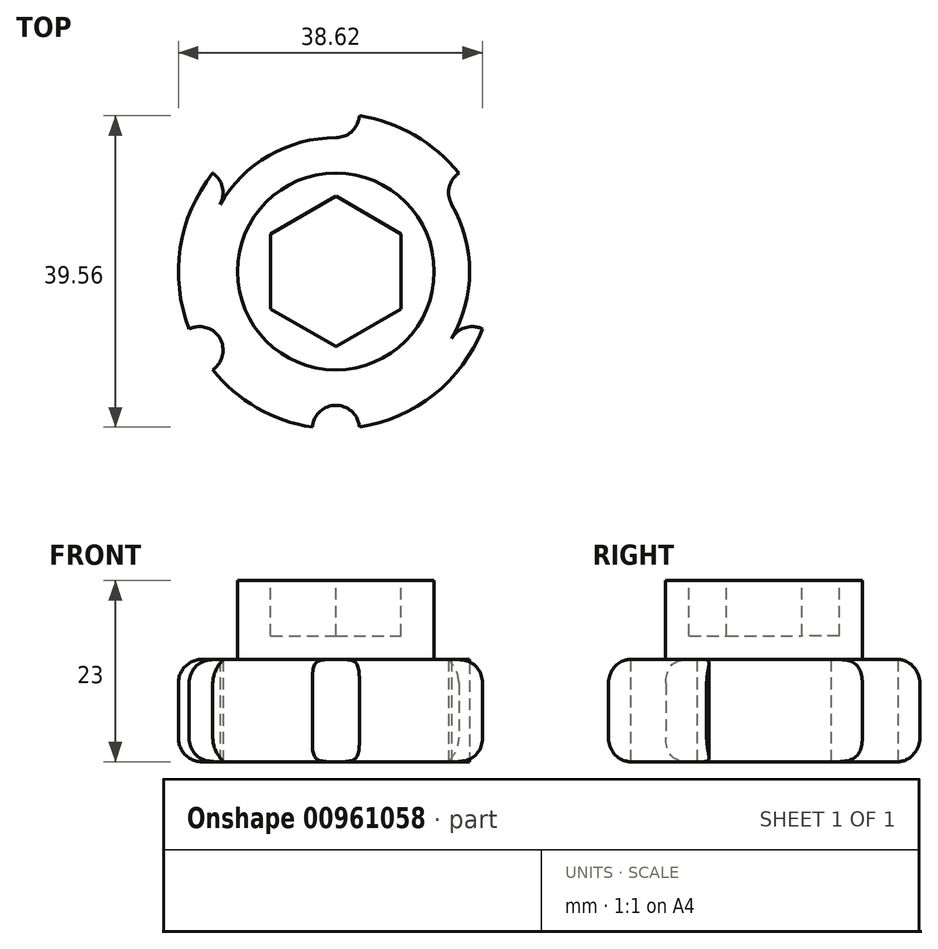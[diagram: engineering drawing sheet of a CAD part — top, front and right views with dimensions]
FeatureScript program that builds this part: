
annotation { "Feature Type Name" : "Feature", "Feature Type Description" : "" }
export const myFeature = defineFeature(function(context is Context, id is Id, definition is map)
    precondition{}
    {
        {
            var Q0;
            Q0=qCreatedBy(makeId("Top.planeOp"),FACE);
            var sketch = newSketch(context, id + "F0", { "sketchPlane" : qUnion([Q0])});
            skCircle(sketch, "E0", {"center": v(0, 0) * mm, "radius": 20 * mm});
            skSolve(sketch);
        }
        {
            var Q0;
            Q0 = qSketchRegion(id + "F0", true);
            extrude(context, id + "F1", {"entities" : qUnion([Q0]), "depth" : 13 * mm, "offsetDistance" : 25 * mm});
        }
        {
            var Q0;
            Q0=makeQuery(id+"F1.opExtrude","CAP_FACE",FACE,{"disambiguationData":[OSD([sQuery(id+"F0.wireOp",EDGE,"E0")])],"isStart":false});
            var sketch = newSketch(context, id + "F2", { "sketchPlane" : qUnion([Q0])});
            skCircle(sketch, "E1", {"center": v(0, 0) * mm, "radius": 12.5 * mm});
            skSolve(sketch);
        }
        {
            var Q0;
            Q0 = qSketchRegion(id + "F2", true);
            extrude(context, id + "F3", {"entities" : qUnion([Q0]), "operationType" : NewBodyOperationType.ADD, "depth" : 10 * mm, "offsetDistance" : 25 * mm});
        }
        {
            var Q0;
            Q0=makeQuery(id+"F1.opExtrude","CAP_EDGE",EDGE,{"disambiguationData":[OSD([sQuery(id+"F0.wireOp",EDGE,"E0")])],"isStart":false});
            var Q1;
            Q1=makeQuery(id+"F1.opExtrude","CAP_EDGE",EDGE,{"disambiguationData":[OSD([sQuery(id+"F0.wireOp",EDGE,"E0")])],"isStart":true});
            fillet(context, id + "F4", {"entities" : qUnion([Q0, Q1]), "radius" : 3 * mm, "tangentPropagation" : true, "allowEdgeOverflow" : false});
        }
        {
            var Q0;
            Q0=makeQuery(id+"F3.opExtrude","CAP_FACE",FACE,{"disambiguationData":[OSD([sQuery(id+"F2.wireOp",EDGE,"E1")])],"isStart":false});
            var sketch = newSketch(context, id + "F5", { "sketchPlane" : qUnion([Q0])});
            skCircle(sketch, "E2.cCircle", {"center": v(0, 0) * mm, "radius": 9.55 * mm, "construction": true});
            skLineSegment(sketch, "E2.0", {"start": v(0, 9.55) * mm, "end": v(8.27, 4.78) * mm});
            skLineSegment(sketch, "E2.1", {"start": v(8.27, 4.78) * mm, "end": v(8.27, -4.77) * mm});
            skLineSegment(sketch, "E2.2", {"start": v(8.27, -4.77) * mm, "end": v(0, -9.55) * mm});
            skLineSegment(sketch, "E2.3", {"start": v(0, -9.55) * mm, "end": v(-8.27, -4.78) * mm});
            skLineSegment(sketch, "E2.4", {"start": v(-8.27, -4.78) * mm, "end": v(-8.27, 4.77) * mm});
            skLineSegment(sketch, "E2.5", {"start": v(-8.27, 4.77) * mm, "end": v(0, 9.55) * mm});
            skSolve(sketch);
        }
        {
            var Q0;
            Q0=makeQuery(id+"F5.imprint","IMPRINT",FACE,{"disambiguationData":[TD([[makeQuery(id+"F5.imprint","IMPRINT",EDGE,{"derivedFrom":sQuery(id+"F5.wireOp",EDGE,"E2.0")}),-1.0]])]});
            extrude(context, id + "F6", {"entities" : qUnion([Q0]), "operationType" : NewBodyOperationType.REMOVE, "oppositeDirection" : true, "depth" : 7 * mm, "offsetDistance" : 25 * mm});
        }
        {
            var Q0;
            Q0=makeQuery(id+"F1.opExtrude","CAP_FACE",FACE,{"disambiguationData":[OSD([sQuery(id+"F0.wireOp",EDGE,"E0")])],"isStart":true});
            var sketch = newSketch(context, id + "F7", { "sketchPlane" : qUnion([Q0])});
            skCircle(sketch, "E3.0", {"center": v(0, 0) * mm, "radius": 20 * mm});
            skCircle(sketch, "E4", {"center": v(0, 20) * mm, "radius": 3 * mm});
            skCircle(sketch, "E5.1.0", {"center": v(-17.32, 10) * mm, "radius": 3 * mm});
            skCircle(sketch, "E5.2.0", {"center": v(-17.32, -10) * mm, "radius": 3 * mm});
            skCircle(sketch, "E5.3.0", {"center": v(0, -20) * mm, "radius": 3 * mm});
            skCircle(sketch, "E5.4.0", {"center": v(17.32, -10) * mm, "radius": 3 * mm});
            skCircle(sketch, "E5.5.0", {"center": v(17.32, 10) * mm, "radius": 3 * mm});
            skSolve(sketch);
        }
        {
            var Q0;
            {var subQ0=sQuery(id+"F7.wireOp",EDGE,"E5.1.0");var subQ1=sQuery(id+"F7.wireOp",EDGE,"E3.0");var subQ2=makeQuery(id+"F7.imprint","INTERSECT",VERTEX,{"disambiguationData":[OD(0.0)],"derivedFrom":[subQ1,subQ0]});Q0=makeQuery(id+"F7.imprint","IMPRINT",FACE,{"disambiguationData":[TD([[makeQuery(id+"F7.imprint","IMPRINT",EDGE,{"disambiguationData":[TD([[subQ2,-1.0]])],"derivedFrom":subQ1}),1.0]])]});}
            var Q1;
            {var subQ0=sQuery(id+"F7.wireOp",EDGE,"E4");var subQ1=sQuery(id+"F7.wireOp",EDGE,"E3.0");var subQ2=makeQuery(id+"F7.imprint","INTERSECT",VERTEX,{"disambiguationData":[OD(0.0)],"derivedFrom":[subQ1,subQ0]});Q1=makeQuery(id+"F7.imprint","IMPRINT",FACE,{"disambiguationData":[TD([[makeQuery(id+"F7.imprint","IMPRINT",EDGE,{"disambiguationData":[TD([[subQ2,-1.0]])],"derivedFrom":subQ1}),1.0]])]});}
            var Q2;
            {var subQ0=sQuery(id+"F7.wireOp",EDGE,"E4");var subQ1=sQuery(id+"F7.wireOp",EDGE,"E3.0");var subQ2=makeQuery(id+"F7.imprint","INTERSECT",VERTEX,{"disambiguationData":[OD(0.0)],"derivedFrom":[subQ1,subQ0]});Q2=makeQuery(id+"F7.imprint","IMPRINT",FACE,{"disambiguationData":[TD([[makeQuery(id+"F7.imprint","IMPRINT",EDGE,{"disambiguationData":[TD([[subQ2,-1.0]])],"derivedFrom":subQ1}),-1.0]])]});}
            var Q3;
            {var subQ0=sQuery(id+"F7.wireOp",EDGE,"E5.1.0");var subQ1=sQuery(id+"F7.wireOp",EDGE,"E3.0");var subQ2=makeQuery(id+"F7.imprint","INTERSECT",VERTEX,{"disambiguationData":[OD(0.0)],"derivedFrom":[subQ1,subQ0]});Q3=makeQuery(id+"F7.imprint","IMPRINT",FACE,{"disambiguationData":[TD([[makeQuery(id+"F7.imprint","IMPRINT",EDGE,{"disambiguationData":[TD([[subQ2,-1.0]])],"derivedFrom":subQ1}),-1.0]])]});}
            var Q4;
            {var subQ0=sQuery(id+"F7.wireOp",EDGE,"E5.2.0");var subQ1=sQuery(id+"F7.wireOp",EDGE,"E3.0");var subQ2=makeQuery(id+"F7.imprint","INTERSECT",VERTEX,{"disambiguationData":[OD(0.0)],"derivedFrom":[subQ1,subQ0]});Q4=makeQuery(id+"F7.imprint","IMPRINT",FACE,{"disambiguationData":[TD([[makeQuery(id+"F7.imprint","IMPRINT",EDGE,{"disambiguationData":[TD([[subQ2,-1.0]])],"derivedFrom":subQ1}),1.0]])]});}
            var Q5;
            {var subQ0=sQuery(id+"F7.wireOp",EDGE,"E5.2.0");var subQ1=sQuery(id+"F7.wireOp",EDGE,"E3.0");var subQ2=makeQuery(id+"F7.imprint","INTERSECT",VERTEX,{"disambiguationData":[OD(0.0)],"derivedFrom":[subQ1,subQ0]});Q5=makeQuery(id+"F7.imprint","IMPRINT",FACE,{"disambiguationData":[TD([[makeQuery(id+"F7.imprint","IMPRINT",EDGE,{"disambiguationData":[TD([[subQ2,-1.0]])],"derivedFrom":subQ1}),-1.0]])]});}
            var Q6;
            {var subQ0=sQuery(id+"F7.wireOp",EDGE,"E5.3.0");var subQ1=sQuery(id+"F7.wireOp",EDGE,"E3.0");var subQ2=makeQuery(id+"F7.imprint","INTERSECT",VERTEX,{"disambiguationData":[OD(0.0)],"derivedFrom":[subQ1,subQ0]});Q6=makeQuery(id+"F7.imprint","IMPRINT",FACE,{"disambiguationData":[TD([[makeQuery(id+"F7.imprint","IMPRINT",EDGE,{"disambiguationData":[TD([[subQ2,-1.0]])],"derivedFrom":subQ1}),1.0]])]});}
            var Q7;
            {var subQ0=sQuery(id+"F7.wireOp",EDGE,"E5.3.0");var subQ1=sQuery(id+"F7.wireOp",EDGE,"E3.0");var subQ2=makeQuery(id+"F7.imprint","INTERSECT",VERTEX,{"disambiguationData":[OD(0.0)],"derivedFrom":[subQ1,subQ0]});Q7=makeQuery(id+"F7.imprint","IMPRINT",FACE,{"disambiguationData":[TD([[makeQuery(id+"F7.imprint","IMPRINT",EDGE,{"disambiguationData":[TD([[subQ2,-1.0]])],"derivedFrom":subQ1}),-1.0]])]});}
            var Q8;
            {var subQ0=sQuery(id+"F7.wireOp",EDGE,"E5.4.0");var subQ1=sQuery(id+"F7.wireOp",EDGE,"E3.0");var subQ2=makeQuery(id+"F7.imprint","INTERSECT",VERTEX,{"disambiguationData":[OD(0.0)],"derivedFrom":[subQ1,subQ0]});Q8=makeQuery(id+"F7.imprint","IMPRINT",FACE,{"disambiguationData":[TD([[makeQuery(id+"F7.imprint","IMPRINT",EDGE,{"disambiguationData":[TD([[subQ2,-1.0]])],"derivedFrom":subQ1}),1.0]])]});}
            var Q9;
            {var subQ0=sQuery(id+"F7.wireOp",EDGE,"E5.4.0");var subQ1=sQuery(id+"F7.wireOp",EDGE,"E3.0");var subQ2=makeQuery(id+"F7.imprint","INTERSECT",VERTEX,{"disambiguationData":[OD(0.0)],"derivedFrom":[subQ1,subQ0]});Q9=makeQuery(id+"F7.imprint","IMPRINT",FACE,{"disambiguationData":[TD([[makeQuery(id+"F7.imprint","IMPRINT",EDGE,{"disambiguationData":[TD([[subQ2,-1.0]])],"derivedFrom":subQ1}),-1.0]])]});}
            var Q10;
            {var subQ0=sQuery(id+"F7.wireOp",EDGE,"E5.5.0");var subQ1=sQuery(id+"F7.wireOp",EDGE,"E3.0");var subQ2=makeQuery(id+"F7.imprint","INTERSECT",VERTEX,{"disambiguationData":[OD(0.0)],"derivedFrom":[subQ1,subQ0]});Q10=makeQuery(id+"F7.imprint","IMPRINT",FACE,{"disambiguationData":[TD([[makeQuery(id+"F7.imprint","IMPRINT",EDGE,{"disambiguationData":[TD([[subQ2,1.0]])],"derivedFrom":subQ1}),1.0]])]});}
            var Q11;
            {var subQ0=sQuery(id+"F7.wireOp",EDGE,"E5.5.0");var subQ1=sQuery(id+"F7.wireOp",EDGE,"E3.0");var subQ2=makeQuery(id+"F7.imprint","INTERSECT",VERTEX,{"disambiguationData":[OD(0.0)],"derivedFrom":[subQ1,subQ0]});Q11=makeQuery(id+"F7.imprint","IMPRINT",FACE,{"disambiguationData":[TD([[makeQuery(id+"F7.imprint","IMPRINT",EDGE,{"disambiguationData":[TD([[subQ2,1.0]])],"derivedFrom":subQ1}),-1.0]])]});}
            extrude(context, id + "F8", {"entities" : qUnion([Q0, Q1, Q2, Q3, Q4, Q5, Q6, Q7, Q8, Q9, Q10, Q11]), "operationType" : NewBodyOperationType.REMOVE, "oppositeDirection" : true, "depth" : 25 * mm, "offsetDistance" : 25 * mm});
        }
    });
